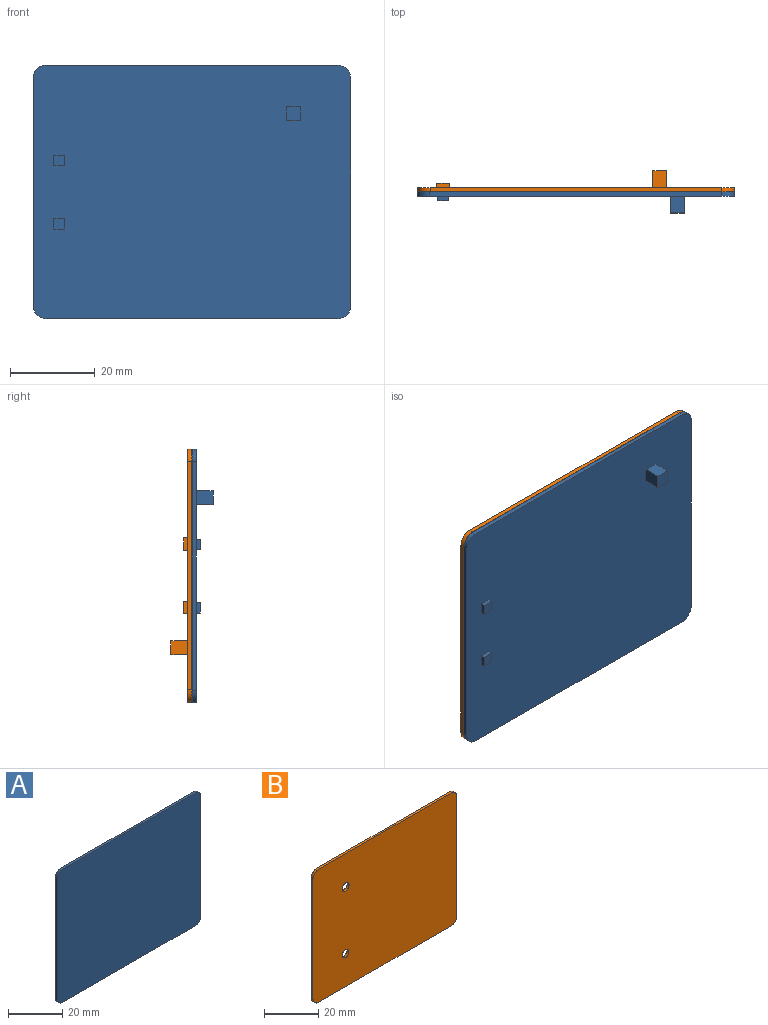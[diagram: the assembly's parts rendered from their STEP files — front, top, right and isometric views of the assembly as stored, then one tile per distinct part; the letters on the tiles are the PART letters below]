
ASSEMBLY  parts=2 mates=1
PART A: 25 faces, bbox 75x5x60 mm
  f0: plane 75x60mm, normal (0,1,0), area 4469mm2, adj f1,f2,f3,f4,f5,f6,f7,f8
  f1: plane 54x1mm, normal (1,0,0), area 54mm2, adj f0,f2,f8,f9
  f2: cylinder r=3mm len=3mm, axis (0,-1,0), area 4.7mm2, adj f0,f1,f3,f9
  f3: plane 69x1mm, normal (0,0,1), area 69mm2, adj f0,f2,f4,f9
  f4: cylinder r=3mm len=3mm, axis (0,-1,0), area 4.7mm2, adj f0,f3,f5,f9
  f5: plane 54x1mm, normal (-1,0,0), area 54mm2, adj f0,f4,f6,f9
  f6: cylinder r=3mm len=2.99mm, axis (0,-1,0), area 4.5mm2, adj f0,f5,f7,f9
  f7: plane 69.21x1mm, normal (0,0,-1), area 69.2mm2, adj f0,f6,f8,f9
  f8: cylinder r=3mm len=3mm, axis (0,-1,0), area 4.7mm2, adj f0,f1,f7,f9
  f9: plane 75x60mm, normal (0,-1,0), area 4492mm2, adj f1,f2,f3,f4,f5,f6,f7,f8
  f10: plane 2.5x1mm, normal (1,0,0), area 2.5mm2, adj f0,f11,f13,f14
  f11: plane 2.5x1mm, normal (0,0,1), area 2.5mm2, adj f0,f10,f12,f14
  f12: plane 2.5x1mm, normal (-1,0,0), area 2.5mm2, adj f0,f11,f13,f14
  f13: plane 2.5x1mm, normal (0,0,-1), area 2.5mm2, adj f0,f10,f12,f14
  f14: plane 2.5x2.5mm, normal (0,1,0), area 6.3mm2, adj f10,f11,f12,f13
  f15: plane 2.5x1mm, normal (1,0,0), area 2.5mm2, adj f0,f16,f18,f19
  f16: plane 2.5x1mm, normal (0,0,1), area 2.5mm2, adj f0,f15,f17,f19
  f17: plane 2.5x1mm, normal (-1,0,0), area 2.5mm2, adj f0,f16,f18,f19
  f18: plane 2.5x1mm, normal (0,0,-1), area 2.5mm2, adj f0,f15,f17,f19
  f19: plane 2.5x2.5mm, normal (0,1,0), area 6.3mm2, adj f15,f16,f17,f18
  f20: plane 4x3.2mm, normal (0,0,-1), area 12.8mm2, adj f0,f21,f23,f24
  f21: plane 4x3.3mm, normal (1,0,0), area 13.2mm2, adj f0,f20,f22,f24
  f22: plane 4x3.2mm, normal (0,0,1), area 12.8mm2, adj f0,f21,f23,f24
  f23: plane 4x3.3mm, normal (-1,0,0), area 13.2mm2, adj f0,f20,f22,f24
  f24: plane 3.3x3.2mm, normal (0,1,0), area 10.6mm2, adj f20,f21,f22,f23
PART B: 27 faces, bbox 75x5x59.9 mm
  f0: plane 75x59.94mm, normal (0,1,0), area 4438.9mm2, adj f1,f2,f3,f4,f5,f6,f7,f8
  f1: cylinder r=3.01mm len=3mm, axis (0,-1,0), area 4.7mm2, adj f0,f2,f10,f11
  f2: plane 54.01x1mm, normal (-1,0,0), area 54mm2, adj f0,f1,f3,f11
  f3: cylinder r=3.01mm len=3mm, axis (0,-1,0), area 4.7mm2, adj f0,f2,f4,f11
  f4: plane 69x1mm, normal (0,0,-1), area 69mm2, adj f0,f3,f5,f11
  f5: cylinder r=3.01mm len=3mm, axis (0,-1,0), area 4.7mm2, adj f0,f4,f6,f11
  f6: plane 54.01x1mm, normal (1,0,0), area 54mm2, adj f0,f5,f7,f11
  f7: cylinder r=3.01mm len=3mm, axis (0,-1,0), area 4.7mm2, adj f0,f6,f10,f11
  f8: cylinder r=1.75mm len=3.5mm, axis (0,-1,0), area 11mm2, adj f0,f11
  f9: cylinder r=1.8mm len=3.6mm, axis (0,-1,0), area 11.3mm2, adj f0,f11
  f10: plane 69x1mm, normal (0,0,1), area 69mm2, adj f0,f1,f7,f11
  f11: plane 75x59.94mm, normal (0,-1,0), area 4467.4mm2, adj f1,f2,f3,f4,f5,f6,f7,f8
  f12: plane 3x1mm, normal (0,0,1), area 3mm2, adj f0,f13,f15,f16
  f13: plane 3x1mm, normal (-1,0,0), area 3mm2, adj f0,f12,f14,f16
  f14: plane 3x1mm, normal (0,0,-1), area 3mm2, adj f0,f13,f15,f16
  f15: plane 3x1mm, normal (1,0,0), area 3mm2, adj f0,f12,f14,f16
  f16: plane 3x3mm, normal (0,1,0), area 9mm2, adj f12,f13,f14,f15
  f17: plane 3x1mm, normal (0,0,1), area 3mm2, adj f0,f18,f20,f21
  f18: plane 3x1mm, normal (-1,0,0), area 3mm2, adj f0,f17,f19,f21
  f19: plane 3x1mm, normal (0,0,-1), area 3mm2, adj f0,f18,f20,f21
  f20: plane 3x1mm, normal (1,0,0), area 3mm2, adj f0,f17,f19,f21
  f21: plane 3x3mm, normal (0,1,0), area 9mm2, adj f17,f18,f19,f20
  f22: plane 4x3.3mm, normal (1,0,0), area 13.2mm2, adj f0,f23,f25,f26
  f23: plane 4x3.2mm, normal (0,0,1), area 12.8mm2, adj f0,f22,f24,f26
  f24: plane 4x3.3mm, normal (-1,0,0), area 13.2mm2, adj f0,f23,f25,f26
  f25: plane 4x3.2mm, normal (0,0,-1), area 12.8mm2, adj f0,f22,f24,f26
  f26: plane 3.3x3.2mm, normal (0,1,0), area 10.6mm2, adj f22,f23,f24,f25
PLACE A rot(axis=(1,0,0),180deg) t=(-20.48,17.52,45.26)mm
PLACE B t=(-20.67,17.52,-14.85)mm
MATE fastened A.f6 <-> B.f1  axis (0,1,0) through (-17.48,17.52,42.26)mm
